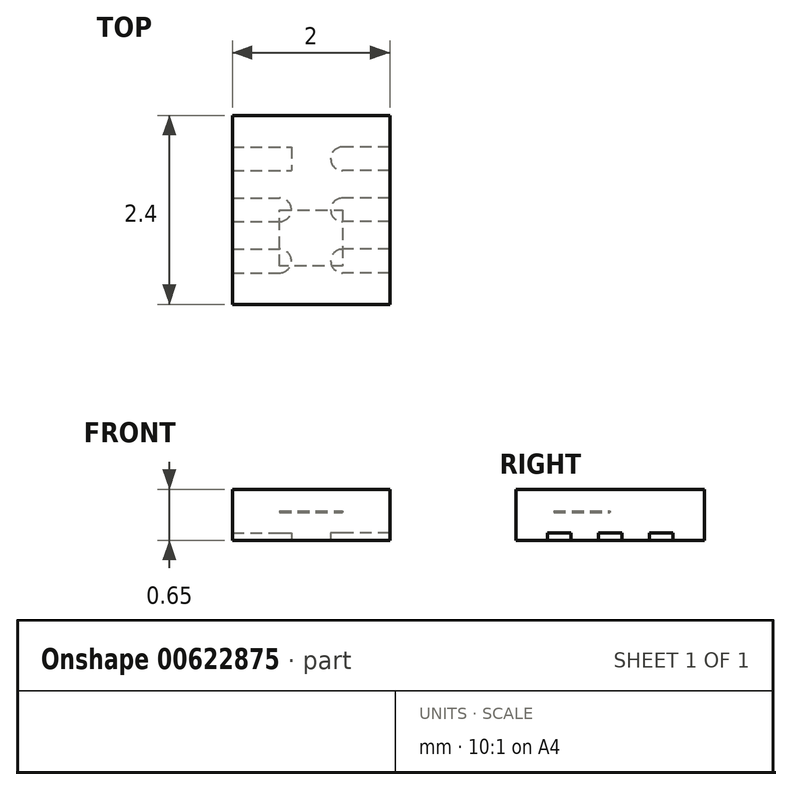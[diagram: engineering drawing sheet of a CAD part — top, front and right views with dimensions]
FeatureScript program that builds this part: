
annotation { "Feature Type Name" : "Feature", "Feature Type Description" : "" }
export const myFeature = defineFeature(function(context is Context, id is Id, definition is map)
    precondition{}
    {
        {
            var Q0;
            Q0=qCreatedBy(makeId("Top.planeOp"),FACE);
            var sketch = newSketch(context, id + "F0", { "sketchPlane" : qUnion([Q0])});
            skLineSegment(sketch, "E0.bottom", {"start": v(0, 0) * mm, "end": v(-2, 0) * mm});
            skLineSegment(sketch, "E0.top", {"start": v(0, 2.4) * mm, "end": v(-2, 2.4) * mm});
            skLineSegment(sketch, "E0.left", {"start": v(0, 0) * mm, "end": v(0, 2.4) * mm});
            skLineSegment(sketch, "E0.right", {"start": v(-2, 0) * mm, "end": v(-2, 2.4) * mm});
            skLineSegment(sketch, "E1.bottom", {"start": v(-2, 2) * mm, "end": v(-1.25, 2) * mm});
            skLineSegment(sketch, "E1.top", {"start": v(-2, 1.7) * mm, "end": v(-1.25, 1.7) * mm});
            skLineSegment(sketch, "E1.left", {"start": v(-2, 2) * mm, "end": v(-2, 1.7) * mm});
            skLineSegment(sketch, "E1.right", {"start": v(-1.25, 2) * mm, "end": v(-1.25, 1.7) * mm});
            skLineSegment(sketch, "E2.bottom", {"start": v(-2, 1.05) * mm, "end": v(-1.4, 1.05) * mm});
            skLineSegment(sketch, "E2.top", {"start": v(-2, 1.35) * mm, "end": v(-1.4, 1.35) * mm});
            skLineSegment(sketch, "E2.left", {"start": v(-2, 1.05) * mm, "end": v(-2, 1.35) * mm});
            skLineSegment(sketch, "E2.right", {"start": v(-1.25, 1.2) * mm, "end": v(-1.25, 1.2) * mm});
            skLineSegment(sketch, "E3.bottom", {"start": v(-2, 0.4) * mm, "end": v(-1.4, 0.4) * mm});
            skLineSegment(sketch, "E3.top", {"start": v(-2, 0.7) * mm, "end": v(-1.4, 0.7) * mm});
            skLineSegment(sketch, "E3.left", {"start": v(-2, 0.4) * mm, "end": v(-2, 0.7) * mm});
            skLineSegment(sketch, "E3.right", {"start": v(-1.25, 0.55) * mm, "end": v(-1.25, 0.55) * mm});
            skLineSegment(sketch, "E4.bottom", {"start": v(0, 0.4) * mm, "end": v(-0.6, 0.4) * mm});
            skLineSegment(sketch, "E4.top", {"start": v(0, 0.7) * mm, "end": v(-0.6, 0.7) * mm});
            skLineSegment(sketch, "E4.left", {"start": v(0, 0.4) * mm, "end": v(0, 0.7) * mm});
            skLineSegment(sketch, "E4.right", {"start": v(-0.75, 0.55) * mm, "end": v(-0.75, 0.55) * mm});
            skLineSegment(sketch, "E5.bottom", {"start": v(0, 1.05) * mm, "end": v(-0.6, 1.05) * mm});
            skLineSegment(sketch, "E5.top", {"start": v(0, 1.35) * mm, "end": v(-0.6, 1.35) * mm});
            skLineSegment(sketch, "E5.left", {"start": v(0, 1.05) * mm, "end": v(0, 1.35) * mm});
            skLineSegment(sketch, "E5.right", {"start": v(-0.75, 1.2) * mm, "end": v(-0.75, 1.2) * mm});
            skLineSegment(sketch, "E6.bottom", {"start": v(0, 1.7) * mm, "end": v(-0.6, 1.7) * mm});
            skLineSegment(sketch, "E6.top", {"start": v(0, 2) * mm, "end": v(-0.6, 2) * mm});
            skLineSegment(sketch, "E6.left", {"start": v(0, 1.7) * mm, "end": v(0, 2) * mm});
            skLineSegment(sketch, "E6.right", {"start": v(-0.75, 1.85) * mm, "end": v(-0.75, 1.85) * mm});
            skPoint(sketch, "E7.visualSharp", {"position": v(-1.25, 1.05) * mm});
            skArc(sketch, "E7.filletArc", {"start": v(-1.4, 1.05) * mm, "mid": v(-1.3, 1.1) * mm, "end": v(-1.25, 1.2) * mm});
            skPoint(sketch, "E8.visualSharp", {"position": v(-1.25, 1.35) * mm});
            skArc(sketch, "E8.filletArc", {"start": v(-1.25, 1.2) * mm, "mid": v(-1.3, 1.3) * mm, "end": v(-1.4, 1.35) * mm});
            skPoint(sketch, "E9.visualSharp", {"position": v(-1.25, 0.4) * mm});
            skArc(sketch, "E9.filletArc", {"start": v(-1.4, 0.4) * mm, "mid": v(-1.3, 0.44) * mm, "end": v(-1.25, 0.55) * mm});
            skPoint(sketch, "E10.visualSharp", {"position": v(-1.25, 0.7) * mm});
            skArc(sketch, "E10.filletArc", {"start": v(-1.25, 0.55) * mm, "mid": v(-1.3, 0.66) * mm, "end": v(-1.4, 0.7) * mm});
            skPoint(sketch, "E11.visualSharp", {"position": v(-0.75, 0.4) * mm});
            skArc(sketch, "E11.filletArc", {"start": v(-0.75, 0.55) * mm, "mid": v(-0.7, 0.44) * mm, "end": v(-0.6, 0.4) * mm});
            skPoint(sketch, "E12.visualSharp", {"position": v(-0.75, 0.7) * mm});
            skArc(sketch, "E12.filletArc", {"start": v(-0.6, 0.7) * mm, "mid": v(-0.7, 0.66) * mm, "end": v(-0.75, 0.55) * mm});
            skPoint(sketch, "E13.visualSharp", {"position": v(-0.75, 1.05) * mm});
            skArc(sketch, "E13.filletArc", {"start": v(-0.75, 1.2) * mm, "mid": v(-0.7, 1.1) * mm, "end": v(-0.6, 1.05) * mm});
            skPoint(sketch, "E14.visualSharp", {"position": v(-0.75, 1.35) * mm});
            skArc(sketch, "E14.filletArc", {"start": v(-0.6, 1.35) * mm, "mid": v(-0.7, 1.3) * mm, "end": v(-0.75, 1.2) * mm});
            skPoint(sketch, "E15.visualSharp", {"position": v(-0.75, 1.7) * mm});
            skArc(sketch, "E15.filletArc", {"start": v(-0.75, 1.85) * mm, "mid": v(-0.7, 1.74) * mm, "end": v(-0.6, 1.7) * mm});
            skPoint(sketch, "E16.visualSharp", {"position": v(-0.75, 2) * mm});
            skArc(sketch, "E16.filletArc", {"start": v(-0.6, 2) * mm, "mid": v(-0.7, 1.96) * mm, "end": v(-0.75, 1.85) * mm});
            skSolve(sketch);
        }
        {
            var Q0;
            Q0=makeQuery(id+"F0.imprint","IMPRINT",FACE,{"disambiguationData":[TD([[makeQuery(id+"F0.imprint","IMPRINT",EDGE,{"derivedFrom":sQuery(id+"F0.wireOp",EDGE,"E0.bottom")}),-1.0]])]});
            var Q1;
            Q1=makeQuery(id+"F0.imprint","IMPRINT",FACE,{"disambiguationData":[TD([[makeQuery(id+"F0.imprint","IMPRINT",EDGE,{"derivedFrom":sQuery(id+"F0.wireOp",EDGE,"E1.bottom")}),-1.0]])]});
            var Q2;
            Q2=makeQuery(id+"F0.imprint","IMPRINT",FACE,{"disambiguationData":[TD([[makeQuery(id+"F0.imprint","IMPRINT",EDGE,{"derivedFrom":sQuery(id+"F0.wireOp",EDGE,"E2.bottom")}),1.0]])]});
            var Q3;
            Q3=makeQuery(id+"F0.imprint","IMPRINT",FACE,{"disambiguationData":[TD([[makeQuery(id+"F0.imprint","IMPRINT",EDGE,{"derivedFrom":sQuery(id+"F0.wireOp",EDGE,"E3.bottom")}),1.0]])]});
            var Q4;
            Q4=makeQuery(id+"F0.imprint","IMPRINT",FACE,{"disambiguationData":[TD([[makeQuery(id+"F0.imprint","IMPRINT",EDGE,{"derivedFrom":sQuery(id+"F0.wireOp",EDGE,"E4.bottom")}),-1.0]])]});
            var Q5;
            Q5=makeQuery(id+"F0.imprint","IMPRINT",FACE,{"disambiguationData":[TD([[makeQuery(id+"F0.imprint","IMPRINT",EDGE,{"derivedFrom":sQuery(id+"F0.wireOp",EDGE,"E5.bottom")}),-1.0]])]});
            var Q6;
            Q6=makeQuery(id+"F0.imprint","IMPRINT",FACE,{"disambiguationData":[TD([[makeQuery(id+"F0.imprint","IMPRINT",EDGE,{"derivedFrom":sQuery(id+"F0.wireOp",EDGE,"E6.bottom")}),-1.0]])]});
            extrude(context, id + "F1", {"entities" : qUnion([Q0, Q1, Q2, Q3, Q4, Q5, Q6]), "depth" : 0.65 * mm, "offsetDistance" : 25 * mm});
        }
        {
            var Q0;
            Q0=makeQuery(id+"F0.imprint","IMPRINT",FACE,{"disambiguationData":[TD([[makeQuery(id+"F0.imprint","IMPRINT",EDGE,{"derivedFrom":sQuery(id+"F0.wireOp",EDGE,"E6.bottom")}),-1.0]])]});
            var Q1;
            Q1=makeQuery(id+"F0.imprint","IMPRINT",FACE,{"disambiguationData":[TD([[makeQuery(id+"F0.imprint","IMPRINT",EDGE,{"derivedFrom":sQuery(id+"F0.wireOp",EDGE,"E1.bottom")}),-1.0]])]});
            var Q2;
            Q2=makeQuery(id+"F0.imprint","IMPRINT",FACE,{"disambiguationData":[TD([[makeQuery(id+"F0.imprint","IMPRINT",EDGE,{"derivedFrom":sQuery(id+"F0.wireOp",EDGE,"E5.bottom")}),-1.0]])]});
            var Q3;
            Q3=makeQuery(id+"F0.imprint","IMPRINT",FACE,{"disambiguationData":[TD([[makeQuery(id+"F0.imprint","IMPRINT",EDGE,{"derivedFrom":sQuery(id+"F0.wireOp",EDGE,"E4.bottom")}),-1.0]])]});
            var Q4;
            Q4=makeQuery(id+"F0.imprint","IMPRINT",FACE,{"disambiguationData":[TD([[makeQuery(id+"F0.imprint","IMPRINT",EDGE,{"derivedFrom":sQuery(id+"F0.wireOp",EDGE,"E2.bottom")}),1.0]])]});
            var Q5;
            Q5=makeQuery(id+"F0.imprint","IMPRINT",FACE,{"disambiguationData":[TD([[makeQuery(id+"F0.imprint","IMPRINT",EDGE,{"derivedFrom":sQuery(id+"F0.wireOp",EDGE,"E3.bottom")}),1.0]])]});
            extrude(context, id + "F2", {"entities" : qUnion([Q0, Q1, Q2, Q3, Q4, Q5]), "depth" : 0.1 * mm, "offsetDistance" : 25 * mm});
        }
        {
            var Q0;
            {var subQ13=sQuery(id+"F0.wireOp",EDGE,"E0.bottom");Q0=makeQuery(id+"F0.imprint","IMPRINT",FACE,{"disambiguationData":[TD([[makeQuery(id+"F0.imprint","IMPRINT",EDGE,{"derivedFrom":subQ13}),-1.0]])]});}
            cPlane(context, id + "F3", {"entities" : qUnion([Q0]), "cplaneType" : CPlaneType.OFFSET, "offset" : 0.35 * mm, "width" : 150 * mm, "height" : 150 * mm});
        }
        {
            var Q0;
            Q0=qCreatedBy(id+"F3.planeOp",FACE);
            var sketch = newSketch(context, id + "F4", { "sketchPlane" : qUnion([Q0])});
            skLineSegment(sketch, "E17", {"start": v(-1.4, 1.2) * mm, "end": v(-0.6, 1.2) * mm});
            skLineSegment(sketch, "E18", {"start": v(-0.6, 1.2) * mm, "end": v(-0.6, 0.48) * mm});
            skLineSegment(sketch, "E19", {"start": v(-0.6, 0.48) * mm, "end": v(-1.4, 0.48) * mm});
            skLineSegment(sketch, "E20", {"start": v(-1.4, 0.48) * mm, "end": v(-1.4, 1.2) * mm});
            skSolve(sketch);
        }
        {
            var Q0;
            Q0=makeQuery(id+"F4.imprint","IMPRINT",FACE,{"disambiguationData":[TD([[makeQuery(id+"F4.imprint","IMPRINT",EDGE,{"derivedFrom":sQuery(id+"F4.wireOp",EDGE,"E17")}),-1.0]])]});
            var Q1;
            Q1=sQuery(id+"F4.wireOp",EDGE,"E18");
            var Q2;
            Q2=sQuery(id+"F4.wireOp",EDGE,"E17");
            var Q3;
            Q3=sQuery(id+"F4.wireOp",EDGE,"E20");
            var Q4;
            Q4=sQuery(id+"F4.wireOp",EDGE,"E19");
            extrude(context, id + "F5", {"entities" : qUnion([Q0]), "surfaceEntities" : qUnion([Q1, Q2, Q3, Q4]), "depth" : 0.02 * mm, "offsetDistance" : 25 * mm});
        }
    });
